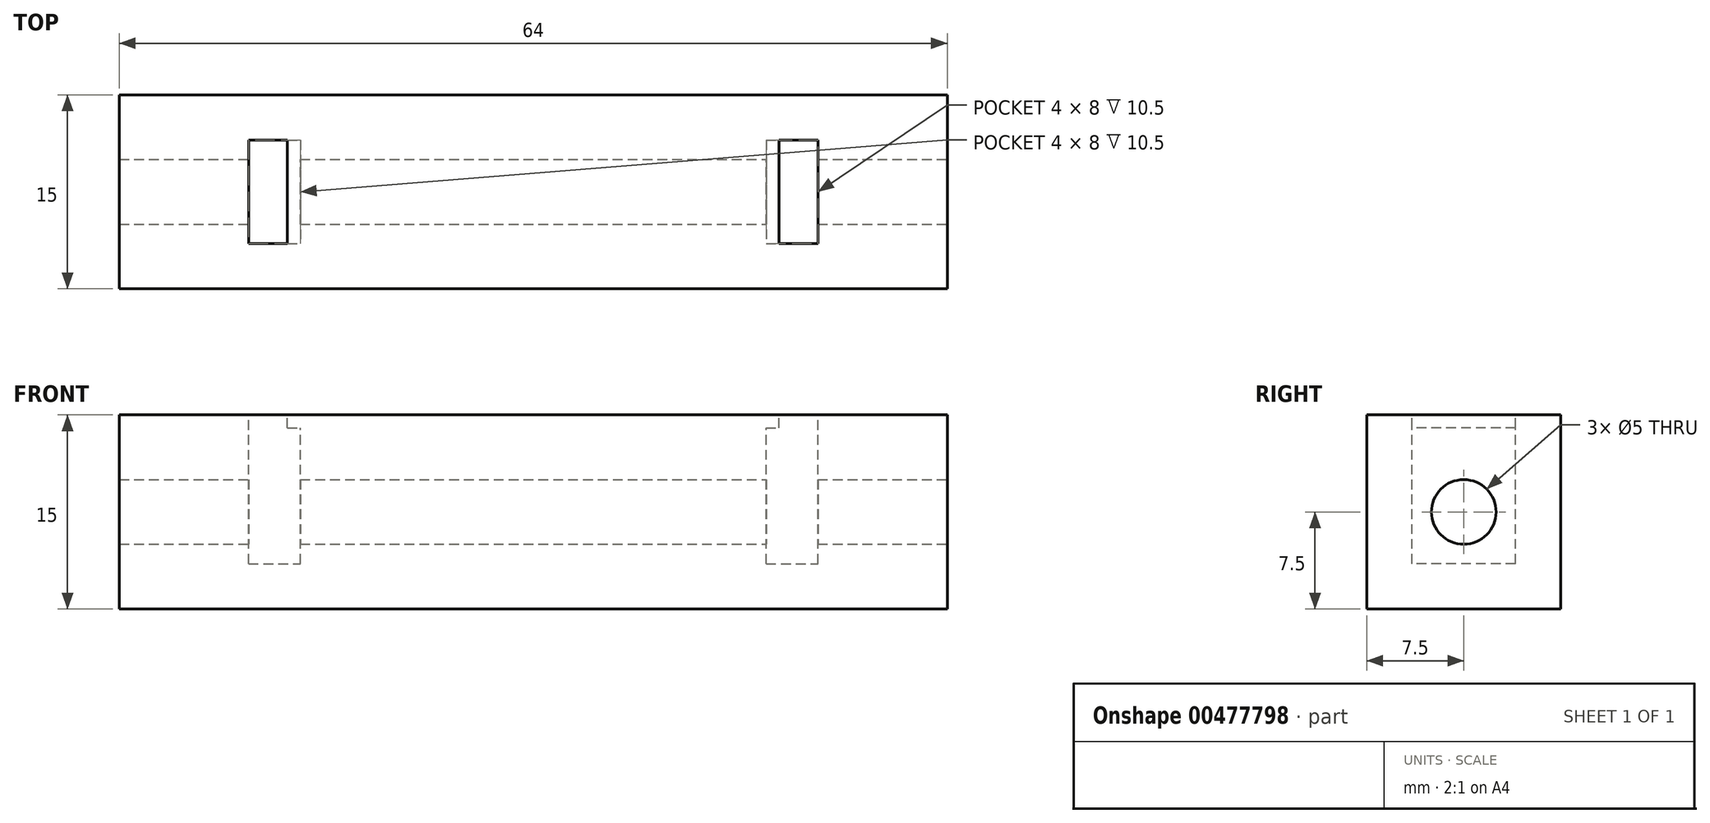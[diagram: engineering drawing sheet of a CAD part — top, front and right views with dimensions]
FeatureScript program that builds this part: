
annotation { "Feature Type Name" : "Feature", "Feature Type Description" : "" }
export const myFeature = defineFeature(function(context is Context, id is Id, definition is map)
    precondition{}
    {
        {
            var Q0;
            Q0=qCreatedBy(makeId("Top.planeOp"),FACE);
            var sketch = newSketch(context, id + "F0", { "sketchPlane" : qUnion([Q0])});
            skLineSegment(sketch, "E0.bottom", {"start": v(0, 0) * mm, "end": v(64, 0) * mm});
            skLineSegment(sketch, "E0.top", {"start": v(0, 15) * mm, "end": v(64, 15) * mm});
            skLineSegment(sketch, "E0.left", {"start": v(0, 0) * mm, "end": v(0, 15) * mm});
            skLineSegment(sketch, "E0.right", {"start": v(64, 0) * mm, "end": v(64, 15) * mm});
            skSolve(sketch);
        }
        {
            var Q0;
            Q0 = qSketchRegion(id + "F0", true);
            extrude(context, id + "F1", {"entities" : qUnion([Q0]), "depth" : 15 * mm, "offsetDistance" : 25 * mm});
        }
        {
            var Q0;
            Q0=makeQuery(id+"F1.opExtrude","SWEPT_FACE",FACE,{"disambiguationData":[OSD([sQuery(id+"F0.wireOp",EDGE,"E0.right")])]});
            var sketch = newSketch(context, id + "F2", { "sketchPlane" : qUnion([Q0])});
            skCircle(sketch, "E1", {"center": v(7.5, 7.5) * mm, "radius": 2.5 * mm});
            skPoint(sketch, "E1.centerSnap0", {"position": v(0, 7.5) * mm});
            skPoint(sketch, "E1.centerSnap1", {"position": v(7.5, 15) * mm});
            skSolve(sketch);
        }
        {
            var Q0;
            Q0 = qSketchRegion(id + "F2", true);
            extrude(context, id + "F3", {"entities" : qUnion([Q0]), "operationType" : NewBodyOperationType.REMOVE, "endBound" : BoundingType.THROUGH_ALL, "oppositeDirection" : true, "depth" : 25 * mm, "offsetDistance" : 25 * mm});
        }
        {
            var Q0;
            Q0=makeQuery(id+"F1.opExtrude","CAP_FACE",FACE,{"disambiguationData":[OSD([sQuery(id+"F0.wireOp",EDGE,"E0.bottom"),sQuery(id+"F0.wireOp",EDGE,"E0.top"),sQuery(id+"F0.wireOp",EDGE,"E0.left"),sQuery(id+"F0.wireOp",EDGE,"E0.right")])],"isStart":false});
            var sketch = newSketch(context, id + "F4", { "sketchPlane" : qUnion([Q0])});
            skLineSegment(sketch, "E2.bottom", {"start": v(10, 11.5) * mm, "end": v(14, 11.5) * mm});
            skLineSegment(sketch, "E2.top", {"start": v(10, 3.5) * mm, "end": v(14, 3.5) * mm});
            skLineSegment(sketch, "E2.left", {"start": v(10, 11.5) * mm, "end": v(10, 3.5) * mm});
            skLineSegment(sketch, "E2.right", {"start": v(14, 11.5) * mm, "end": v(14, 3.5) * mm});
            skLineSegment(sketch, "E3.bottom", {"start": v(50, 11.5) * mm, "end": v(54, 11.5) * mm});
            skLineSegment(sketch, "E3.top", {"start": v(50, 3.5) * mm, "end": v(54, 3.5) * mm});
            skLineSegment(sketch, "E3.left", {"start": v(50, 11.5) * mm, "end": v(50, 3.5) * mm});
            skLineSegment(sketch, "E3.right", {"start": v(54, 11.5) * mm, "end": v(54, 3.5) * mm});
            skSolve(sketch);
        }
        {
            var Q0;
            Q0 = qSketchRegion(id + "F4", true);
            extrude(context, id + "F5", {"entities" : qUnion([Q0]), "operationType" : NewBodyOperationType.REMOVE, "oppositeDirection" : true, "depth" : 11.5 * mm, "offsetDistance" : 25 * mm});
        }
        {
            var Q0;
            Q0=makeQuery(id+"F1.opExtrude","CAP_FACE",FACE,{"disambiguationData":[OSD([sQuery(id+"F0.wireOp",EDGE,"E0.bottom"),sQuery(id+"F0.wireOp",EDGE,"E0.top"),sQuery(id+"F0.wireOp",EDGE,"E0.left"),sQuery(id+"F0.wireOp",EDGE,"E0.right")])],"isStart":false});
            var sketch = newSketch(context, id + "F6", { "sketchPlane" : qUnion([Q0])});
            skLineSegment(sketch, "E4.bottom", {"start": v(14, 3.5) * mm, "end": v(13, 3.5) * mm});
            skLineSegment(sketch, "E4.top", {"start": v(14, 11.5) * mm, "end": v(13, 11.5) * mm});
            skLineSegment(sketch, "E4.left", {"start": v(14, 3.5) * mm, "end": v(14, 11.5) * mm});
            skLineSegment(sketch, "E4.right", {"start": v(13, 3.5) * mm, "end": v(13, 11.5) * mm});
            skLineSegment(sketch, "E5.bottom", {"start": v(50, 3.5) * mm, "end": v(51, 3.5) * mm});
            skLineSegment(sketch, "E5.top", {"start": v(50, 11.5) * mm, "end": v(51, 11.5) * mm});
            skLineSegment(sketch, "E5.left", {"start": v(50, 3.5) * mm, "end": v(50, 11.5) * mm});
            skLineSegment(sketch, "E5.right", {"start": v(51, 3.5) * mm, "end": v(51, 11.5) * mm});
            skSolve(sketch);
        }
        {
            var Q0;
            Q0 = qSketchRegion(id + "F6", true);
            extrude(context, id + "F7", {"entities" : qUnion([Q0]), "operationType" : NewBodyOperationType.ADD, "oppositeDirection" : true, "depth" : 1 * mm, "offsetDistance" : 25 * mm});
        }
    });
